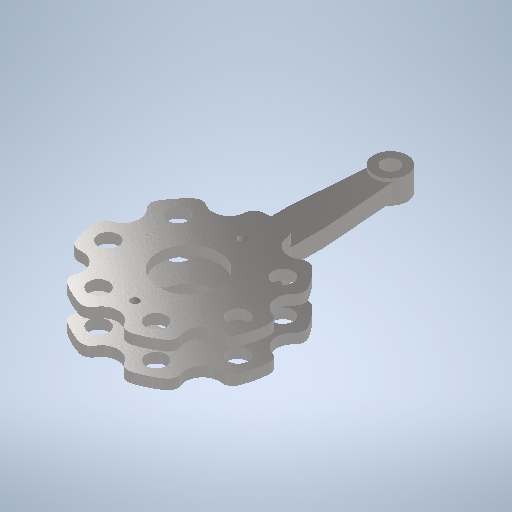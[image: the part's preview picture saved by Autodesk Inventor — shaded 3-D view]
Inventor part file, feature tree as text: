
AUTODESK INVENTOR PART (.ipt)
format: ipt  version: 2025 (Build 290162010, 162A)  size: 499,712 bytes
history: native  units: mm
features: sketch x10, extrude x6, plane x4, hole x4, projected_geometry x3, pattern_circular x2, fillet x1
ambient origin geometry x8: Origin, YZ Plane, XZ Plane, XY Plane, X Axis, Y Axis, Z Axis, Center Point
bodies: Volumenkörper3 (feature_tree)
feature tree (30):
  extrude  "Extrusion7"  Depth=10.0mm
  plane  "Arbeitsebene3"
  extrude  "Extrusion8"  TaperAngle=0.0deg  [1 undecoded]
  plane  "Arbeitsebene8"
  extrude  "Extrusion10"  Depth=13.0mm TaperAngle=0.0deg
  plane  "Arbeitsebene9"
  extrude  "Extrusion11"  Depth=7.0mm
  hole  "Bohrung4"  [1 undecoded]
  hole  "Bohrung5"  [1 undecoded]
  extrude  "Extrusion12"  Depth=10.0mm TaperAngle=0.0deg
  fillet  "Rundung3"  Radius=3.0mm
  pattern_circular  "Runde Anordnung5"  Count=7 Angle=360.0deg
  plane  "Arbeitsebene5"
  hole  "Bohrung9"  [1 undecoded]
  pattern_circular  "Runde Anordnung6"  [2 undecoded]
  hole  "Bohrung8"  [1 undecoded]
  extrude  "Extrusion13"  Depth=10.0mm
  sketch  "Skizze13"  dims[d62=13.0mm d63=10.0mm]
  sketch  "Skizze14"  dims[d64=5.0mm d65=0.0mm d66=0.0mm]
  sketch  "Skizze16"  dims[d68=52.0mm d69=13.0mm d70=0.0mm]
  projected_geometry  "Projizierte Kontur3"
  sketch  "Skizze17"  dims[d75=7.0mm d76=60.0mm]
  sketch  "Skizze18"  dims[d77=30.619976mm d78=5.0mm d79=0.0mm]
  sketch  "Skizze19"  dims[d81=7.0mm d82=0.0mm]
  projected_geometry  "Projizierte Kontur4"
  sketch  "Skizze20"  dims[d83=5.0mm d84=6.0mm d85=4.0mm d86=2.0mm d87=90.0deg d88=8.0mm d89=0.0mm d90=21.0mm]
  sketch  "Skizze22"  dims[d91=5.0mm d92=10.0mm d93=0.0mm d94=3.0mm d95=70.0mm d96=360.0deg]
  sketch  "Skizze25"  dims[d99=-52.0mm d100=7.0mm]
  sketch  "Skizze27"  dims[d101=52.0mm d102=52.0mm d103=0.0mm d104=18.0mm d105=6.0mm d106=4.0mm d107=2.0mm d108=90.0deg d109=8.0mm d110=0.0mm d126=60.0mm d127=44.680429mm d129=10.0mm d130=2.459mm d131=6.0mm d132=4.0mm d133=2.0mm d134=90.0deg d135=8.0mm d136=20.594885mm d137=32.0mm d143=0.0mm d144=40.0mm d145=6.0mm d146=6.0mm d147=4.0mm d148=2.0mm d149=90.0deg d150=8.0mm d151=0.0mm d152=0.0mm d153=10.0mm]
  projected_geometry  "Projizierte Kontur6"
note: 7 required parameter values undecoded (feature->parameter linkage not recoverable at this tier; creation-order binding heuristic only, values carry confidence <= 0.55)
